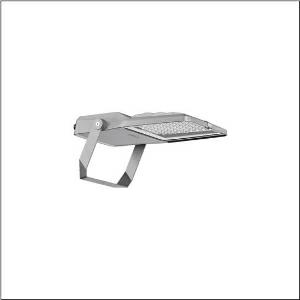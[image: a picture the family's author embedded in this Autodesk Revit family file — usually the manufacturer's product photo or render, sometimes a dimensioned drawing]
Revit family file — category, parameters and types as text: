
# Revit family: floodlight_fl_21_mini___pl61_5xa7776c2c1a_8570
name_source: partatom
category: Lighting Fixtures
units: mm (PartAtom-declared; Revit-internal decimal feet)

## family parameters
Cut with Voids When Loaded = No
Host = Face
Light Source = No
Part Type = Normal
Room Calculation Point = No
Round Connector Dimension = Use Diameter
Shared = No

## types (1)
- --- (1 x LED, 11960 lm, 89 W, 3000K)
    Apparent Load = 89 VA
    CIE Flux Codes = 33 65 98 100 100
    Color Rendering = 70
    Color Temperature = 3000K
    Default Elevation = 1800 mm
    Description = Floodlight FL 21 mini, floodlight, primary light control with lens, of PMMA, primary optical cover: protective disc, of toughened safety glass, transparent, light distribution: PL61, light emission: direct distribution, installation type: surface-mounted, LED, High Power LED, rated luminous flux: 11.960lm, luminous efficacy: 134lm/W, light colour: 730, colour temperature: 3000K, control gear: Smart Interface (Zhaga), control: flexible luminous flux parameterisation, time-dependent luminous flux control, constant luminous flux control, overheat protection, pre-setting: logarithmic dimming characteristic, with terminal, 6-pole, mains connection: 220..240V, AC, 50/60Hz, start of lifetime: 89W, end of service life: 94W, reduction: 43W, luminaire housing, of diecast aluminium, powder-coated, Siteco® metallic grey (DB 702S), corrosivity category C5 mid according to DIN EN ISO 12944, suitable for swimming pools, chlorine-resistant, sealing non-destructively replaceable, mounting bracket, of steel, galvanised, powder-coated, Siteco® metallic grey (DB 702S), Smart Interface below and above, protection rating (complete): IP66, insulation class (complete): insulation class II (safety insulation), certification: CE, ENEC, VDE, protection symbol: D, impact resistance: IK08, permissible operating ambient temperature: -40..+40°C, permissible operating ambient temperature for outdoor applications: -40..+50°C, standard: DIN EN 12944, LABS conformity tested according to VDMA 24364:2018-05, packaging unit: 1 piece

Light Distribution: PL61
    Height = 70 mm
    Lamp = 1 x LED
    Lamp Light Flux = 11960 lm
    Lamp Power = 89 W
    Lamp count = 1
    Length = 485 mm
    Luminous efficacy = 134 lm/W
    Manufacturer = Siteco
    ModVariant = No
    Model = 5XA7776C2C1A
    Number of Poles = 1
    OnlyDefault = Yes
    Power Factor = 1
    Product Name = Floodlight FL 21 mini | PL61
    Product group = floodlight | pylon annexe
    ProductGroupID = 6200
    Protection Class = Protection class II
    Protection Degree = IP 66
    RLX_Detail_Level = 1
    RLX_Emergency_Light_Flux = 0 lm
    RLX_Emergency_Type = 0
    RLX_Emergency_Type_DB = No
    RlxData = <blob elided: 96033 chars, md5=efbcebd0>
    Socket = socket
    Standby Power = 0 W
    System Light Flux = 11960 lm
    System Power = 89 W
    Type Comments = factory setting: luminous flux: 100 % | dim-lin: 254 | 456 mA
    Type Image = l_1006845.jpg
    URL = http://relux.com
    VarID = @adj_172030
    Voltage = 0 V
    Weight = 0.00 kg
    Width = 337 mm

## geometry (parser evidence)
native form markers: Blend x4, Sweep x10
no freeform markers — native parametric forms only
